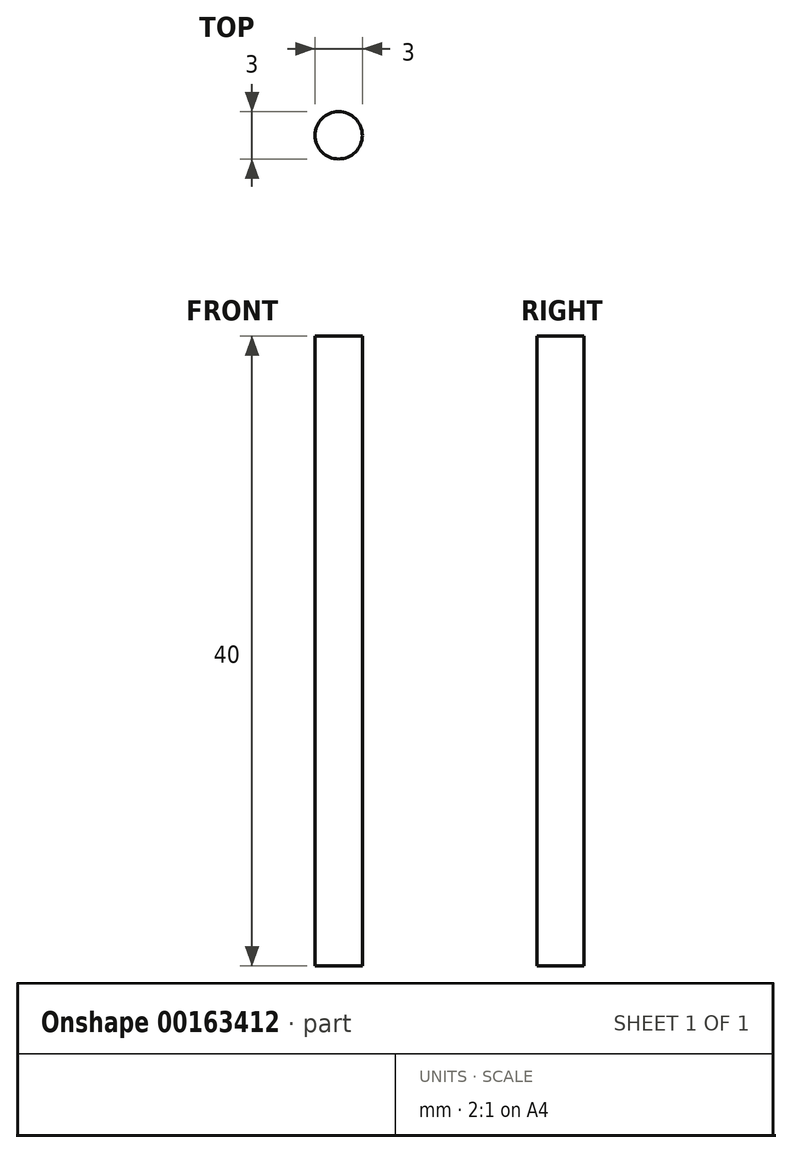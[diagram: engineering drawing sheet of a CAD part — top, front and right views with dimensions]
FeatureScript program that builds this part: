
annotation { "Feature Type Name" : "Feature", "Feature Type Description" : "" }
export const myFeature = defineFeature(function(context is Context, id is Id, definition is map)
    precondition{}
    {
        {
            var Q0;
            Q0=qCreatedBy(makeId("Top.planeOp"),FACE);
            var sketch = newSketch(context, id + "F0", { "sketchPlane" : qUnion([Q0])});
            skCircle(sketch, "E0", {"center": v(0, 0) * mm, "radius": 1.5 * mm});
            skSolve(sketch);
        }
        {
            var Q0;
            Q0 = qSketchRegion(id + "F0", true);
            var Q1;
            Q1=sQuery(id+"F0.wireOp",EDGE,"E0");
            extrude(context, id + "F1", {"entities" : qUnion([Q0]), "surfaceEntities" : qUnion([Q1]), "depth" : 40 * mm});
        }
    });
